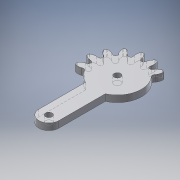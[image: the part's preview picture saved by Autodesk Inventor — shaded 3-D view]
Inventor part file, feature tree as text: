
AUTODESK INVENTOR PART (.ipt)
format: ipt  version: 2016 (Build 200138000, 138)  size: 419,840 bytes
history: native  units: mm
features: extrude x8, sketch x4, fillet x2, pattern_circular x1
ambient origin geometry x8: Origin, YZ Plane, XZ Plane, XY Plane, X Axis, Y Axis, Z Axis, Center Point
bodies: Solid1 (feature_tree)
feature tree (15):
  sketch  "Sketch1"  dims[d0=3.0mm d1=0.0mm d2=10.0mm d3=0.0mm]
  extrude  "Extrusion1"  Depth=10.0mm TaperAngle=0.0deg
  extrude  "Extrusion2"  Depth=150.0mm TaperAngle=360.0deg
  fillet  "Fillet1"  Radius=9.0mm
  pattern_circular  "Circular Pattern1"  [2 undecoded]
  sketch  "Sketch3"  dims[d4=0.2mm d5=150.0mm d6=360.0deg d9=9.0mm]
  extrude  "Extrusion3"  Depth=31.1mm
  extrude  "Extrusion4"  Depth=31.1mm TaperAngle=0.0deg
  extrude  "Extrusion5"  TaperAngle=150.0deg  [1 undecoded]
  extrude  "Extrusion6"  Depth=31.1mm TaperAngle=0.0deg
  extrude  "Extrusion7"  Depth=3.0mm
  fillet  "Fillet5"  Radius=10.0mm
  extrude  "Extrusion10"  Depth=4.5mm
  sketch  "Sketch7"  dims[d10=3.0mm]
  sketch  "Sketch10"  dims[d11=35.6mm d12=0.0mm d13=45.0mm d14=0.0mm d15=7.295476mm d16=45.0mm d17=0.0mm d18=150.0deg d19=45.0mm d20=0.0mm d21=3.0mm d22=10.0mm d23=0.0mm d33=4.5mm d34=3.0mm d35=10.0mm d36=0.0mm d37=31.1mm]
note: 3 required parameter values undecoded (feature->parameter linkage not recoverable at this tier; creation-order binding heuristic only, values carry confidence <= 0.55)
